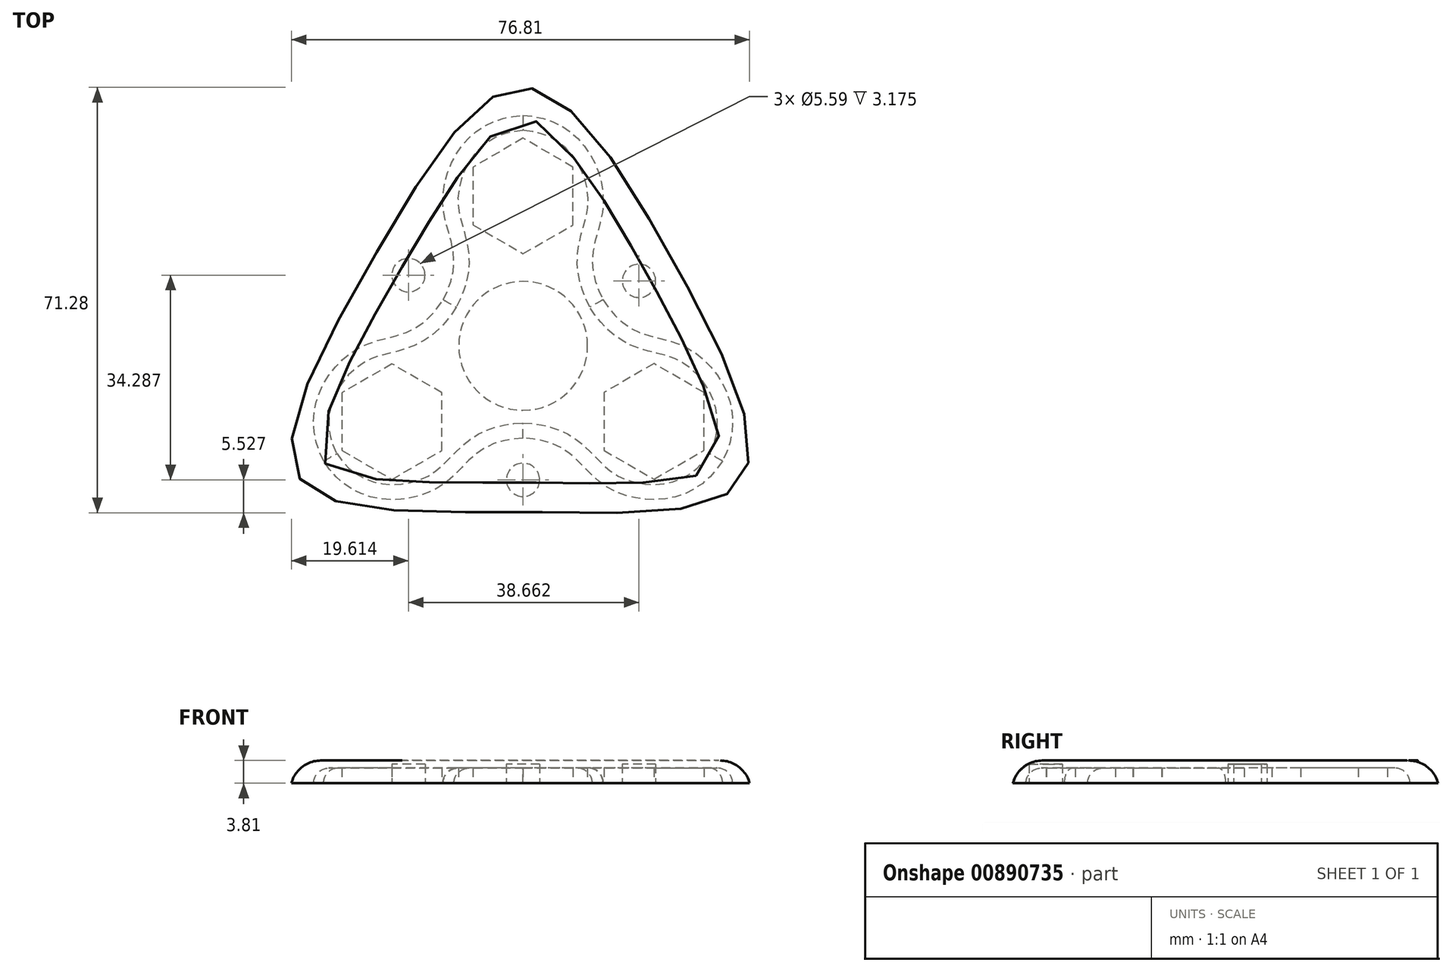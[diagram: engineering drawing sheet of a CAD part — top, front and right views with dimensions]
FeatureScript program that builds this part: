
annotation { "Feature Type Name" : "Feature", "Feature Type Description" : "" }
export const myFeature = defineFeature(function(context is Context, id is Id, definition is map)
    precondition{}
    {
        {
            var Q0;
            Q0=qCreatedBy(makeId("Top.planeOp"),FACE);
            var sketch = newSketch(context, id + "F0", { "sketchPlane" : qUnion([Q0])});
            skCircle(sketch, "E0", {"center": v(0, 0) * mm, "radius": 10.8 * mm});
            skLineSegment(sketch, "E1", {"start": v(0, 0) * mm, "end": v(0, 25.1) * mm, "construction": true});
            skLineSegment(sketch, "E2", {"start": v(0, 0) * mm, "end": v(21.74, 12.55) * mm, "construction": true});
            skLineSegment(sketch, "E3", {"start": v(0, 0) * mm, "end": v(21.94, -12.67) * mm, "construction": true});
            skLineSegment(sketch, "E4", {"start": v(0, 0) * mm, "end": v(0, -25.1) * mm, "construction": true});
            skLineSegment(sketch, "E5", {"start": v(0, 0) * mm, "end": v(-22, -12.7) * mm, "construction": true});
            skLineSegment(sketch, "E6", {"start": v(0, 0) * mm, "end": v(-21.74, 12.55) * mm, "construction": true});
            skCircle(sketch, "E7.cCircle", {"center": v(0, 25.1) * mm, "radius": 8.38 * mm, "construction": true});
            skLineSegment(sketch, "E7.0", {"start": v(8.38, 29.95) * mm, "end": v(8.38, 20.27) * mm});
            skLineSegment(sketch, "E7.1", {"start": v(8.38, 20.27) * mm, "end": v(0, 15.43) * mm});
            skLineSegment(sketch, "E7.2", {"start": v(0, 15.43) * mm, "end": v(-8.38, 20.27) * mm});
            skLineSegment(sketch, "E7.3", {"start": v(-8.38, 20.27) * mm, "end": v(-8.38, 29.95) * mm});
            skLineSegment(sketch, "E7.4", {"start": v(-8.38, 29.95) * mm, "end": v(0, 34.79) * mm});
            skLineSegment(sketch, "E7.5", {"start": v(0, 34.79) * mm, "end": v(8.38, 29.95) * mm});
            skPoint(sketch, "E7.0.midPoint", {"position": v(8.38, 25.1) * mm});
            skCircle(sketch, "E8.cCircle", {"center": v(21.94, -12.67) * mm, "radius": 8.38 * mm, "construction": true});
            skLineSegment(sketch, "E8.0", {"start": v(13.55, -17.5) * mm, "end": v(13.55, -7.83) * mm});
            skLineSegment(sketch, "E8.1", {"start": v(13.55, -7.83) * mm, "end": v(21.94, -2.99) * mm});
            skLineSegment(sketch, "E8.2", {"start": v(21.94, -2.99) * mm, "end": v(30.32, -7.83) * mm});
            skLineSegment(sketch, "E8.3", {"start": v(30.32, -7.83) * mm, "end": v(30.32, -17.5) * mm});
            skLineSegment(sketch, "E8.4", {"start": v(30.32, -17.5) * mm, "end": v(21.94, -22.34) * mm});
            skLineSegment(sketch, "E8.5", {"start": v(21.94, -22.34) * mm, "end": v(13.55, -17.5) * mm});
            skPoint(sketch, "E8.0.midPoint", {"position": v(13.55, -12.67) * mm});
            skCircle(sketch, "E9.cCircle", {"center": v(-22, -12.7) * mm, "radius": 8.38 * mm, "construction": true});
            skLineSegment(sketch, "E9.0", {"start": v(-13.6, -7.86) * mm, "end": v(-13.6, -17.54) * mm});
            skLineSegment(sketch, "E9.1", {"start": v(-13.6, -17.54) * mm, "end": v(-22, -22.38) * mm});
            skLineSegment(sketch, "E9.2", {"start": v(-22, -22.38) * mm, "end": v(-30.37, -17.54) * mm});
            skLineSegment(sketch, "E9.3", {"start": v(-30.37, -17.54) * mm, "end": v(-30.37, -7.86) * mm});
            skLineSegment(sketch, "E9.4", {"start": v(-30.37, -7.86) * mm, "end": v(-22, -3.02) * mm});
            skLineSegment(sketch, "E9.5", {"start": v(-22, -3.02) * mm, "end": v(-13.6, -7.86) * mm});
            skPoint(sketch, "E9.0.midPoint", {"position": v(-13.6, -12.7) * mm});
            skFitSpline(sketch, "E10", {"points": [v(0, 38.6) * mm, v(13.45, 23.73) * mm, v(13.39, 7.73) * mm], "startDerivative": vector(54.84, -2.13) * mm, "endDerivative": vector(24.96, -47.54) * mm});
            skFitSpline(sketch, "E11.MirrorCS", {"points": [v(33.44, -19.3) * mm, v(27.28, -0.22) * mm, v(13.39, 7.73) * mm], "startDerivative": vector(25.58, 48.55) * mm, "endDerivative": vector(-28.7, 45.38) * mm});
            skFitSpline(sketch, "E12.MirrorCS", {"points": [v(33.44, -19.3) * mm, v(13.83, -23.51) * mm, v(0, -15.46) * mm], "startDerivative": vector(-29.26, -46.43) * mm, "endDerivative": vector(-53.65, 2.16) * mm});
            skFitSpline(sketch, "E13.MirrorCS", {"points": [v(-33.44, -19.3) * mm, v(-13.83, -23.51) * mm, v(0, -15.46) * mm], "startDerivative": vector(29.26, -46.43) * mm, "endDerivative": vector(53.65, 2.16) * mm});
            skFitSpline(sketch, "E14.MirrorCS", {"points": [v(-33.44, -19.3) * mm, v(-27.28, -0.22) * mm, v(-13.39, 7.73) * mm], "startDerivative": vector(-25.58, 48.55) * mm, "endDerivative": vector(28.7, 45.38) * mm});
            skFitSpline(sketch, "E15.MirrorCS", {"points": [v(0, 38.6) * mm, v(-13.45, 23.73) * mm, v(-13.39, 7.73) * mm], "startDerivative": vector(-54.84, -2.13) * mm, "endDerivative": vector(-24.96, -47.54) * mm});
            skSolve(sketch);
        }
        {
            var Q0;
            Q0=makeQuery(id+"F0.imprint","IMPRINT",FACE,{"disambiguationData":[TD([[makeQuery(id+"F0.imprint","IMPRINT",EDGE,{"derivedFrom":sQuery(id+"F0.wireOp",EDGE,"E0")}),-1.0]])]});
            extrude(context, id + "F1", {"entities" : qUnion([Q0]), "endBound" : BoundingType.SYMMETRIC, "depth" : 5.08 * mm, "offsetDistance" : 25.4 * mm});
        }
        {
            var Q0;
            Q0=makeQuery(id+"F1.opExtrude","CAP_EDGE",EDGE,{"disambiguationData":[OSD([sQuery(id+"F0.wireOp",EDGE,"E13.MirrorCS")])],"isStart":false});
            var Q1;
            Q1=makeQuery(id+"F1.opExtrude","CAP_EDGE",EDGE,{"disambiguationData":[OSD([sQuery(id+"F0.wireOp",EDGE,"E12.MirrorCS")])],"isStart":false});
            var Q2;
            Q2=makeQuery(id+"F1.opExtrude","CAP_EDGE",EDGE,{"disambiguationData":[OSD([sQuery(id+"F0.wireOp",EDGE,"E11.MirrorCS")])],"isStart":false});
            var Q3;
            Q3=makeQuery(id+"F1.opExtrude","CAP_EDGE",EDGE,{"disambiguationData":[OSD([sQuery(id+"F0.wireOp",EDGE,"E10")])],"isStart":false});
            var Q4;
            Q4=makeQuery(id+"F1.opExtrude","CAP_EDGE",EDGE,{"disambiguationData":[OSD([sQuery(id+"F0.wireOp",EDGE,"E15.MirrorCS")])],"isStart":false});
            var Q5;
            Q5=makeQuery(id+"F1.opExtrude","CAP_EDGE",EDGE,{"disambiguationData":[OSD([sQuery(id+"F0.wireOp",EDGE,"E14.MirrorCS")])],"isStart":false});
            var Q6;
            Q6=makeQuery(id+"F1.opExtrude","CAP_EDGE",EDGE,{"disambiguationData":[OSD([sQuery(id+"F0.wireOp",EDGE,"E13.MirrorCS")])],"isStart":true});
            var Q7;
            Q7=makeQuery(id+"F1.opExtrude","CAP_EDGE",EDGE,{"disambiguationData":[OSD([sQuery(id+"F0.wireOp",EDGE,"E12.MirrorCS")])],"isStart":true});
            var Q8;
            Q8=makeQuery(id+"F1.opExtrude","CAP_EDGE",EDGE,{"disambiguationData":[OSD([sQuery(id+"F0.wireOp",EDGE,"E11.MirrorCS")])],"isStart":true});
            var Q9;
            Q9=makeQuery(id+"F1.opExtrude","CAP_EDGE",EDGE,{"disambiguationData":[OSD([sQuery(id+"F0.wireOp",EDGE,"E10")])],"isStart":true});
            var Q10;
            Q10=makeQuery(id+"F1.opExtrude","CAP_EDGE",EDGE,{"disambiguationData":[OSD([sQuery(id+"F0.wireOp",EDGE,"E15.MirrorCS")])],"isStart":true});
            var Q11;
            Q11=makeQuery(id+"F1.opExtrude","CAP_EDGE",EDGE,{"disambiguationData":[OSD([sQuery(id+"F0.wireOp",EDGE,"E14.MirrorCS")])],"isStart":true});
            fillet(context, id + "F2", {"entities" : qUnion([Q0, Q1, Q2, Q3, Q4, Q5, Q6, Q7, Q8, Q9, Q10, Q11]), "radius" : 2.54 * mm, "tangentPropagation" : true, "allowEdgeOverflow" : false});
        }
        {
            var Q0;
            Q0=qCreatedBy(makeId("Top.planeOp"),FACE);
            var sketch = newSketch(context, id + "F3", { "sketchPlane" : qUnion([Q0])});
            skFitSpline(sketch, "E16", {"points": [v(-24.52, 15.68) * mm, v(0, 43.3) * mm, v(25.1, 14.34) * mm, v(36.7, -22.45) * mm, v(0, -27.82) * mm, v(-37.72, -21.83) * mm, v(-24.52, 15.68) * mm]});
            skCircle(sketch, "E17", {"center": v(-19.23, 11.83) * mm, "radius": 2.8 * mm});
            skCircle(sketch, "E18", {"center": v(19.44, 10.89) * mm, "radius": 2.8 * mm});
            skCircle(sketch, "E19", {"center": v(0, -22.45) * mm, "radius": 2.8 * mm});
            skSolve(sketch);
        }
        {
            var Q0;
            Q0=makeQuery(id+"F3.imprint","IMPRINT",FACE,{"disambiguationData":[TD([[makeQuery(id+"F3.imprint","IMPRINT",EDGE,{"derivedFrom":sQuery(id+"F3.wireOp",EDGE,"E16")}),-1.0]])]});
            var Q1;
            Q1=makeQuery(id+"F3.imprint","IMPRINT",FACE,{"disambiguationData":[TD([[makeQuery(id+"F3.imprint","IMPRINT",EDGE,{"derivedFrom":sQuery(id+"F3.wireOp",EDGE,"E17")}),1.0]])]});
            var Q2;
            Q2=makeQuery(id+"F3.imprint","IMPRINT",FACE,{"disambiguationData":[TD([[makeQuery(id+"F3.imprint","IMPRINT",EDGE,{"derivedFrom":sQuery(id+"F3.wireOp",EDGE,"E18")}),1.0]])]});
            var Q3;
            Q3=makeQuery(id+"F3.imprint","IMPRINT",FACE,{"disambiguationData":[TD([[makeQuery(id+"F3.imprint","IMPRINT",EDGE,{"derivedFrom":sQuery(id+"F3.wireOp",EDGE,"E19")}),1.0]])]});
            extrude(context, id + "F4", {"entities" : qUnion([Q0, Q1, Q2, Q3]), "depth" : 3.8 * mm, "offsetDistance" : 25.4 * mm});
        }
        {
            var Q0;
            Q0=makeQuery(id+"F3.imprint","IMPRINT",FACE,{"disambiguationData":[TD([[makeQuery(id+"F3.imprint","IMPRINT",EDGE,{"derivedFrom":sQuery(id+"F3.wireOp",EDGE,"E17")}),1.0]])]});
            var Q1;
            Q1=makeQuery(id+"F3.imprint","IMPRINT",FACE,{"disambiguationData":[TD([[makeQuery(id+"F3.imprint","IMPRINT",EDGE,{"derivedFrom":sQuery(id+"F3.wireOp",EDGE,"E18")}),1.0]])]});
            var Q2;
            Q2=makeQuery(id+"F3.imprint","IMPRINT",FACE,{"disambiguationData":[TD([[makeQuery(id+"F3.imprint","IMPRINT",EDGE,{"derivedFrom":sQuery(id+"F3.wireOp",EDGE,"E19")}),1.0]])]});
            extrude(context, id + "F5", {"entities" : qUnion([Q0, Q1, Q2]), "operationType" : NewBodyOperationType.REMOVE, "depth" : 3.17 * mm, "offsetDistance" : 25.4 * mm});
        }
        {
            var Q0;
            Q0=makeQuery(id+"F1.opExtrude","SWEPT_BODY",BODY,{"disambiguationData":[OSD([sQuery(id+"F0.wireOp",EDGE,"E0"),sQuery(id+"F0.wireOp",EDGE,"E7.0"),sQuery(id+"F0.wireOp",EDGE,"E7.1"),sQuery(id+"F0.wireOp",EDGE,"E7.2"),sQuery(id+"F0.wireOp",EDGE,"E7.3"),sQuery(id+"F0.wireOp",EDGE,"E7.4"),sQuery(id+"F0.wireOp",EDGE,"E7.5"),sQuery(id+"F0.wireOp",EDGE,"E8.0"),sQuery(id+"F0.wireOp",EDGE,"E8.1"),sQuery(id+"F0.wireOp",EDGE,"E8.2"),sQuery(id+"F0.wireOp",EDGE,"E8.3"),sQuery(id+"F0.wireOp",EDGE,"E8.4"),sQuery(id+"F0.wireOp",EDGE,"E8.5"),sQuery(id+"F0.wireOp",EDGE,"E9.0"),sQuery(id+"F0.wireOp",EDGE,"E9.1"),sQuery(id+"F0.wireOp",EDGE,"E9.2"),sQuery(id+"F0.wireOp",EDGE,"E9.3"),sQuery(id+"F0.wireOp",EDGE,"E9.4"),sQuery(id+"F0.wireOp",EDGE,"E9.5"),sQuery(id+"F0.wireOp",EDGE,"E10"),sQuery(id+"F0.wireOp",EDGE,"E11.MirrorCS"),sQuery(id+"F0.wireOp",EDGE,"E12.MirrorCS"),sQuery(id+"F0.wireOp",EDGE,"E13.MirrorCS"),sQuery(id+"F0.wireOp",EDGE,"E14.MirrorCS"),sQuery(id+"F0.wireOp",EDGE,"E15.MirrorCS")])]});
            var Q1;
            Q1=makeQuery(id+"F4.opExtrude","SWEPT_BODY",BODY,{"disambiguationData":[OSD([sQuery(id+"F3.wireOp",EDGE,"E16")])]});
            booleanBodies(context, id + "F6", {"operationType" : BooleanOperationType.SUBTRACTION, "tools" : qUnion([Q0]), "targets" : qUnion([Q1])});
        }
        {
            var Q0;
            Q0=makeQuery(id+"F4.opExtrude","CAP_EDGE",EDGE,{"disambiguationData":[OSD([sQuery(id+"F3.wireOp",EDGE,"E16")])],"isStart":false});
            fillet(context, id + "F7", {"entities" : qUnion([Q0]), "radius" : 5.08 * mm, "tangentPropagation" : true, "allowEdgeOverflow" : false});
        }
    });
